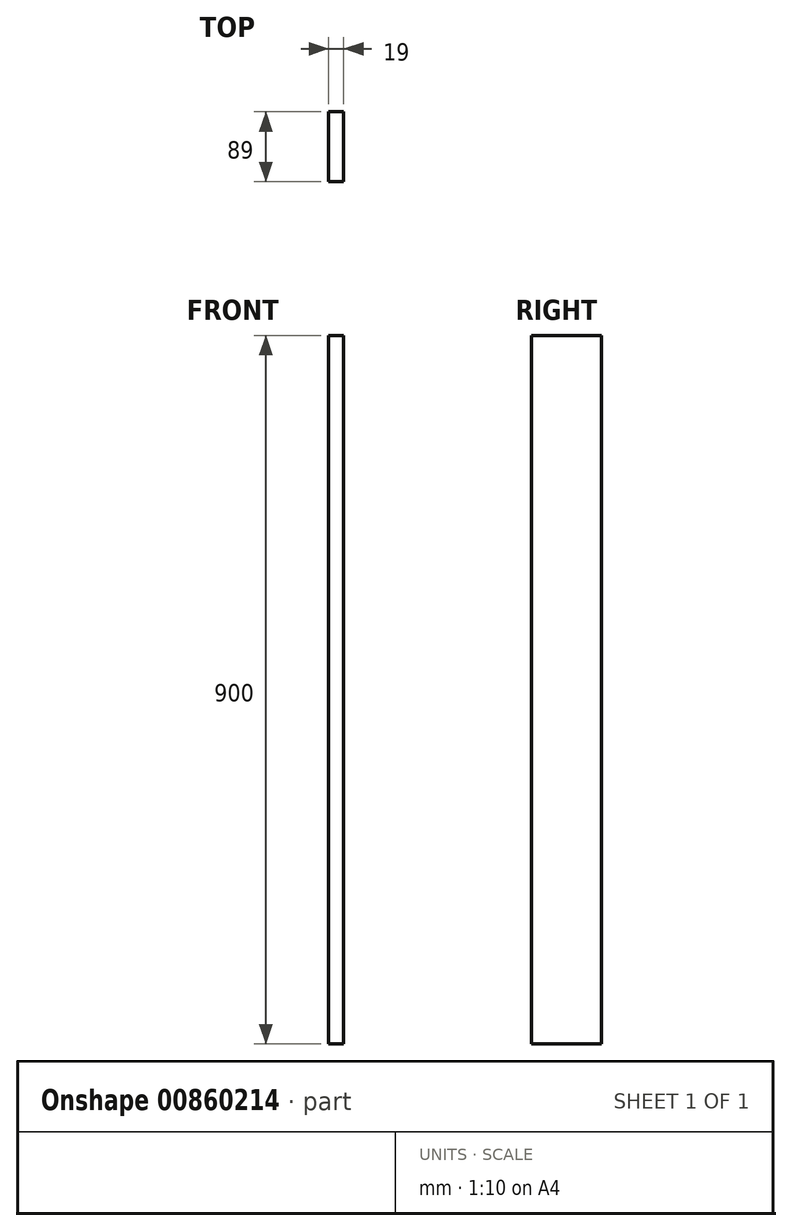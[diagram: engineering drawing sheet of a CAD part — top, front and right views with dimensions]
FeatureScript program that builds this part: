
annotation { "Feature Type Name" : "Feature", "Feature Type Description" : "" }
export const myFeature = defineFeature(function(context is Context, id is Id, definition is map)
    precondition{}
    {
        {
            var Q0;
            Q0=qCreatedBy(makeId("Top.planeOp"),FACE);
            var sketch = newSketch(context, id + "F0", { "sketchPlane" : qUnion([Q0])});
            skLineSegment(sketch, "E0.bottom", {"start": v(0, 0) * mm, "end": v(19, 0) * mm});
            skLineSegment(sketch, "E0.top", {"start": v(0, -89) * mm, "end": v(19, -89) * mm});
            skLineSegment(sketch, "E0.left", {"start": v(0, 0) * mm, "end": v(0, -89) * mm});
            skLineSegment(sketch, "E0.right", {"start": v(19, 0) * mm, "end": v(19, -89) * mm});
            skSolve(sketch);
        }
        {
            var Q0;
            Q0 = qSketchRegion(id + "F0", true);
            extrude(context, id + "F1", {"entities" : qUnion([Q0]), "depth" : 900 * mm, "offsetDistance" : 25 * mm});
        }
    });
